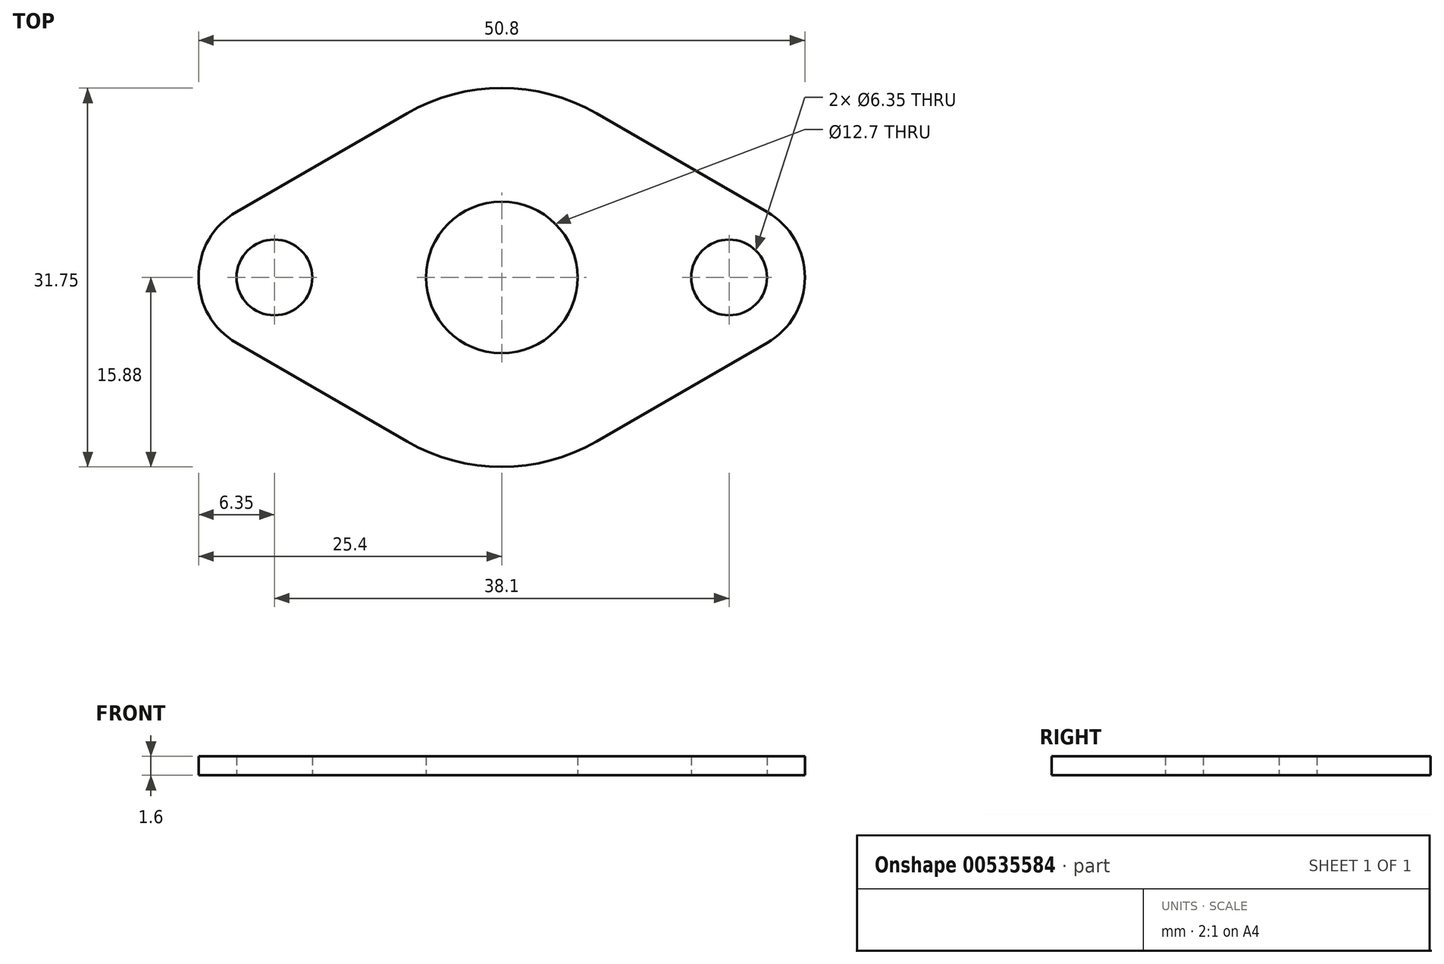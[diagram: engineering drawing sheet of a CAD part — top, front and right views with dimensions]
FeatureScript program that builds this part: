
annotation { "Feature Type Name" : "Feature", "Feature Type Description" : "" }
export const myFeature = defineFeature(function(context is Context, id is Id, definition is map)
    precondition{}
    {
        {
            var Q0;
            Q0=qCreatedBy(makeId("Top.planeOp"),FACE);
            var sketch = newSketch(context, id + "F0", { "sketchPlane" : qUnion([Q0])});
            skCircle(sketch, "E0", {"center": v(0, 0) * mm, "radius": 6.35 * mm});
            skCircle(sketch, "E1", {"center": v(-19.05, 0) * mm, "radius": 3.18 * mm});
            skCircle(sketch, "E2", {"center": v(19.05, 0) * mm, "radius": 3.18 * mm});
            skArc(sketch, "E3", {"start": v(-7.94, -13.75) * mm, "mid": v(0, -15.88) * mm, "end": v(7.94, -13.75) * mm});
            skArc(sketch, "E4", {"start": v(22.23, -5.5) * mm, "mid": v(25.4, 0) * mm, "end": v(22.23, 5.5) * mm});
            skLineSegment(sketch, "E5", {"start": v(0, 0) * mm, "end": v(0, 14.95) * mm, "construction": true});
            skArc(sketch, "E6.MirrorC", {"start": v(-22.23, -5.5) * mm, "mid": v(-25.4, 0) * mm, "end": v(-22.23, 5.5) * mm});
            skLineSegment(sketch, "E7", {"start": v(-22.23, 5.5) * mm, "end": v(-7.94, 13.75) * mm});
            skLineSegment(sketch, "E8", {"start": v(22.22, 5.5) * mm, "end": v(7.94, 13.75) * mm});
            skLineSegment(sketch, "E9", {"start": v(0, 0) * mm, "end": v(-11.23, 0) * mm, "construction": true});
            skLineSegment(sketch, "E10.MirrorCS", {"start": v(22.23, -5.5) * mm, "end": v(7.94, -13.75) * mm});
            skLineSegment(sketch, "E11.MirrorCS", {"start": v(-22.22, -5.5) * mm, "end": v(-7.94, -13.75) * mm});
            skArc(sketch, "E12.trimOffspring", {"start": v(7.94, 13.75) * mm, "mid": v(0, 15.88) * mm, "end": v(-7.94, 13.75) * mm});
            skSolve(sketch);
        }
        {
            var Q0;
            Q0=makeQuery(id+"F0.imprint","IMPRINT",FACE,{"disambiguationData":[TD([[makeQuery(id+"F0.imprint","IMPRINT",EDGE,{"derivedFrom":sQuery(id+"F0.wireOp",EDGE,"E0")}),-1.0]])]});
            extrude(context, id + "F1", {"entities" : qUnion([Q0]), "depth" : 1.6 * mm, "offsetDistance" : 25.4 * mm});
        }
    });
